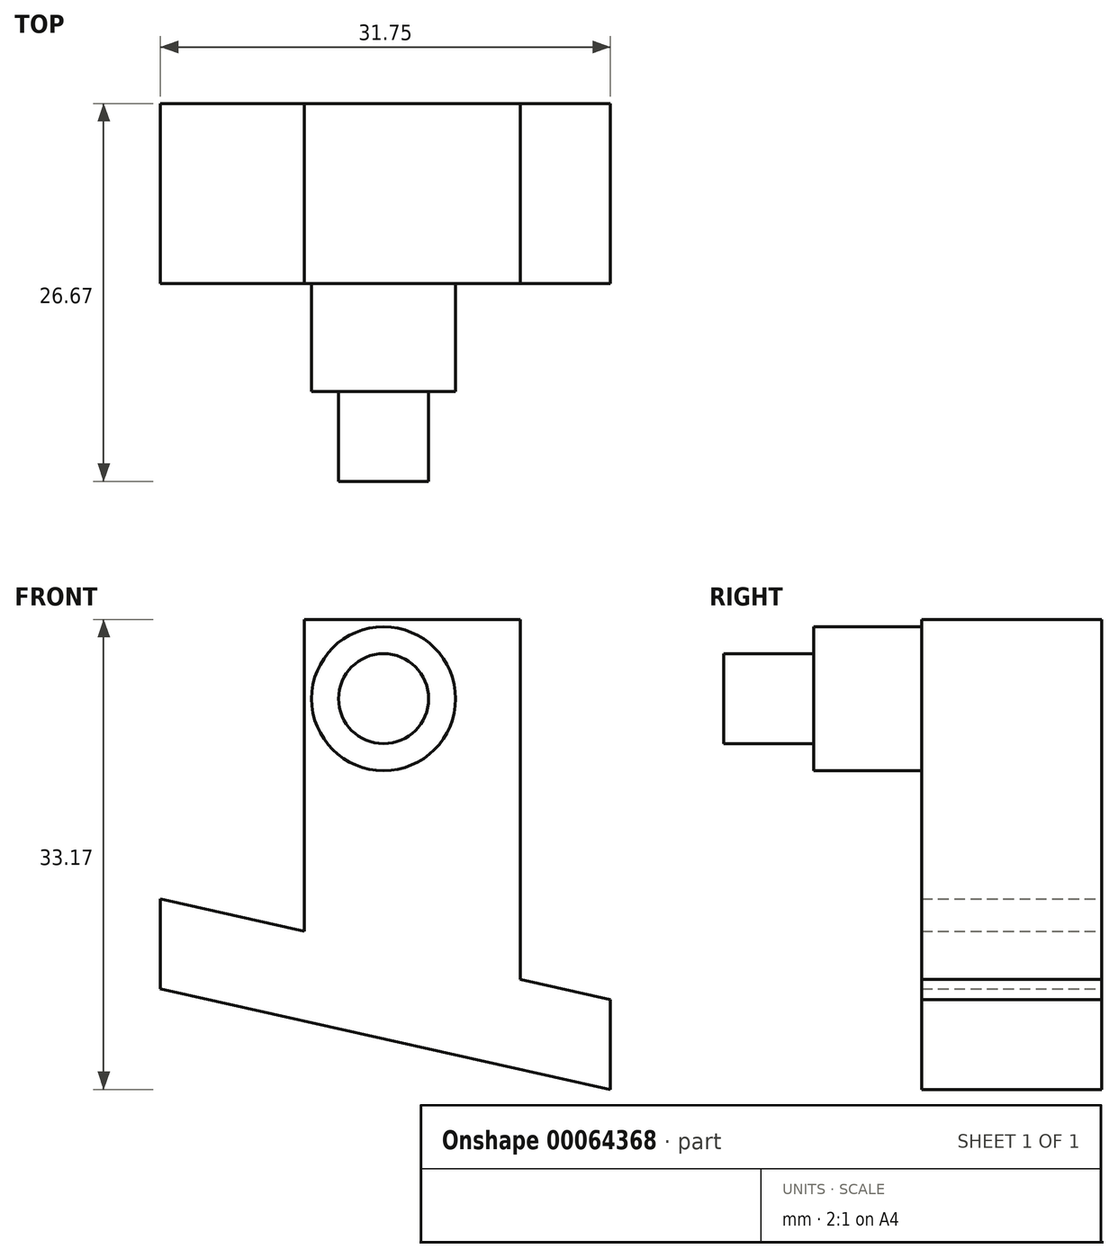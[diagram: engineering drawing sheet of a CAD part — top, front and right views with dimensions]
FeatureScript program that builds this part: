
annotation { "Feature Type Name" : "Feature", "Feature Type Description" : "" }
export const myFeature = defineFeature(function(context is Context, id is Id, definition is map)
    precondition{}
    {
        {
            var Q0;
            Q0=qCreatedBy(makeId("Front.planeOp"),FACE);
            var sketch = newSketch(context, id + "F0", { "sketchPlane" : qUnion([Q0])});
            skLineSegment(sketch, "E0", {"start": v(-14.74, 9.37) * mm, "end": v(17, 2.28) * mm});
            skLineSegment(sketch, "E1", {"start": v(17, 2.28) * mm, "end": v(17, -4.07) * mm});
            skLineSegment(sketch, "E2", {"start": v(17, -4.07) * mm, "end": v(-14.74, 3.02) * mm});
            skLineSegment(sketch, "E3", {"start": v(-14.74, 3.02) * mm, "end": v(-14.74, 9.37) * mm});
            skLineSegment(sketch, "E4", {"start": v(-4.58, 7.1) * mm, "end": v(-4.58, 29.1) * mm});
            skLineSegment(sketch, "E5", {"start": v(-4.58, 29.1) * mm, "end": v(10.66, 29.1) * mm});
            skLineSegment(sketch, "E6", {"start": v(10.66, 29.1) * mm, "end": v(10.66, 3.7) * mm});
            skLineSegment(sketch, "E7", {"start": v(10.66, 3.7) * mm, "end": v(-4.58, 7.1) * mm});
            skSolve(sketch);
        }
        {
            var Q0;
            Q0=makeQuery(id+"F0.imprint","IMPRINT",FACE,{"disambiguationData":[TD([[makeQuery(id+"F0.imprint","IMPRINT",EDGE,{"derivedFrom":sQuery(id+"F0.wireOp",EDGE,"E4")}),-1.0]])]});
            var Q1;
            {var subQ0=sQuery(id+"F0.wireOp",EDGE,"E1");Q1=makeQuery(id+"F0.imprint","IMPRINT",FACE,{"disambiguationData":[TD([[makeQuery(id+"F0.imprint","IMPRINT",EDGE,{"derivedFrom":subQ0}),-1.0]])]});}
            extrude(context, id + "F1", {"entities" : qUnion([Q0, Q1]), "depth" : 12.7 * mm});
        }
        {
            var Q0;
            Q0=makeQuery(id+"F1.opExtrude","CAP_FACE",FACE,{"disambiguationData":[OSD([sQuery(id+"F0.wireOp",EDGE,"E0"),sQuery(id+"F0.wireOp",EDGE,"E1"),sQuery(id+"F0.wireOp",EDGE,"E2"),sQuery(id+"F0.wireOp",EDGE,"E3"),sQuery(id+"F0.wireOp",EDGE,"E4"),sQuery(id+"F0.wireOp",EDGE,"E5"),sQuery(id+"F0.wireOp",EDGE,"E6")])],"isStart":false});
            var sketch = newSketch(context, id + "F2", { "sketchPlane" : qUnion([Q0])});
            skCircle(sketch, "E8", {"center": v(1, 23.5) * mm, "radius": 5.08 * mm});
            skSolve(sketch);
        }
        {
            var Q0;
            Q0=makeQuery(id+"F2.imprint","IMPRINT",FACE,{"disambiguationData":[TD([[makeQuery(id+"F2.imprint","IMPRINT",EDGE,{"derivedFrom":sQuery(id+"F2.wireOp",EDGE,"E8")}),1.0]])]});
            extrude(context, id + "F3", {"entities" : qUnion([Q0]), "operationType" : NewBodyOperationType.ADD, "depth" : 7.62 * mm});
        }
        {
            var Q0;
            Q0=makeQuery(id+"F3.opExtrude","CAP_FACE",FACE,{"disambiguationData":[OSD([sQuery(id+"F2.wireOp",EDGE,"E8")])],"isStart":false});
            var sketch = newSketch(context, id + "F4", { "sketchPlane" : qUnion([Q0])});
            skCircle(sketch, "E9", {"center": v(1, 23.5) * mm, "radius": 3.17 * mm});
            skSolve(sketch);
        }
        {
            var Q0;
            Q0=makeQuery(id+"F4.imprint","IMPRINT",FACE,{"disambiguationData":[TD([[makeQuery(id+"F4.imprint","IMPRINT",EDGE,{"derivedFrom":sQuery(id+"F4.wireOp",EDGE,"E9")}),1.0]])]});
            extrude(context, id + "F5", {"entities" : qUnion([Q0]), "operationType" : NewBodyOperationType.ADD, "depth" : 6.35 * mm});
        }
    });
